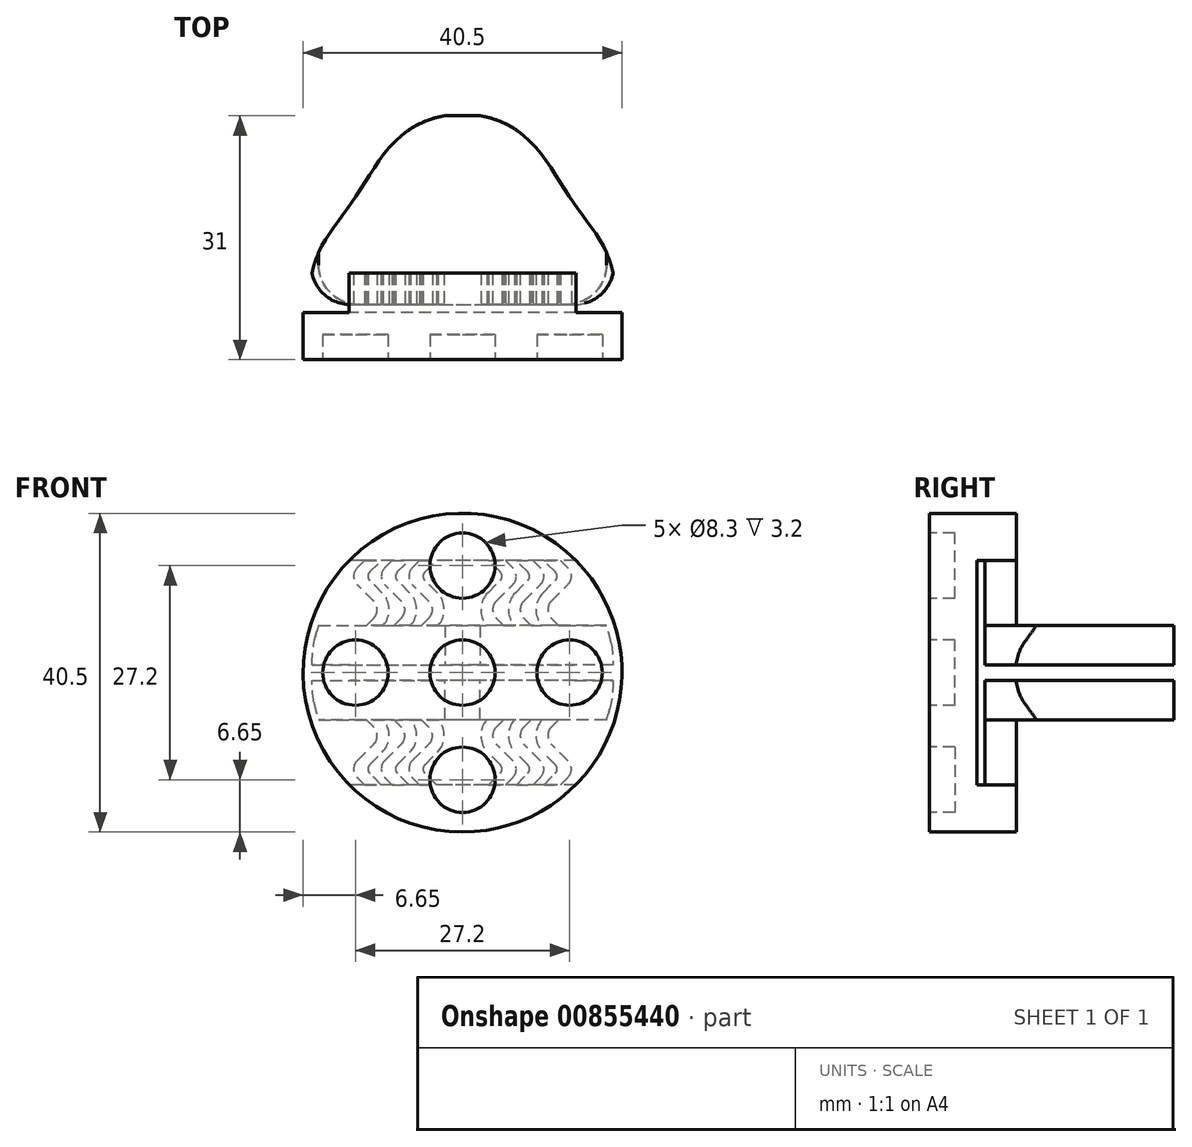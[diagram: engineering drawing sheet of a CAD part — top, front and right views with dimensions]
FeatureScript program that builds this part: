
annotation { "Feature Type Name" : "Feature", "Feature Type Description" : "" }
export const myFeature = defineFeature(function(context is Context, id is Id, definition is map)
    precondition{}
    {
        {
            var Q0;
            Q0=qCreatedBy(makeId("Front.planeOp"),FACE);
            var sketch = newSketch(context, id + "F0", { "sketchPlane" : qUnion([Q0])});
            skCircle(sketch, "E0", {"center": v(0, 0) * mm, "radius": 20.25 * mm});
            skSolve(sketch);
        }
        {
            var Q0;
            Q0 = qSketchRegion(id + "F0", true);
            extrude(context, id + "F1", {"entities" : qUnion([Q0]), "depth" : 6 * mm, "offsetDistance" : 25 * mm});
        }
        {
            var Q0;
            Q0=makeQuery(id+"F1.opExtrude","CAP_FACE",FACE,{"disambiguationData":[OSD([sQuery(id+"F0.wireOp",EDGE,"E0")])],"isStart":false});
            var sketch = newSketch(context, id + "F2", { "sketchPlane" : qUnion([Q0])});
            skCircle(sketch, "E1", {"center": v(0, 0) * mm, "radius": 4.15 * mm});
            skCircle(sketch, "E2", {"center": v(0, 13.6) * mm, "radius": 4.15 * mm});
            skLineSegment(sketch, "E3", {"start": v(-10.79, 17.75) * mm, "end": v(11.03, 17.75) * mm, "construction": true});
            skLineSegment(sketch, "E4", {"start": v(0, 13.6) * mm, "end": v(0, 0) * mm, "construction": true});
            skLineSegment(sketch, "E5", {"start": v(-8.03, 20.25) * mm, "end": v(13.1, 20.25) * mm, "construction": true});
            skCircle(sketch, "E6.1.0", {"center": v(-13.6, 0) * mm, "radius": 4.15 * mm});
            skCircle(sketch, "E6.2.0", {"center": v(0, -13.6) * mm, "radius": 4.15 * mm});
            skCircle(sketch, "E6.3.0", {"center": v(13.6, 0) * mm, "radius": 4.15 * mm});
            skSolve(sketch);
        }
        {
            var Q0;
            Q0 = qSketchRegion(id + "F2", true);
            extrude(context, id + "F3", {"entities" : qUnion([Q0]), "operationType" : NewBodyOperationType.REMOVE, "oppositeDirection" : true, "depth" : 3.2 * mm, "offsetDistance" : 25 * mm});
        }
        {
            var Q0;
            Q0=makeQuery(id+"F1.opExtrude","CAP_FACE",FACE,{"disambiguationData":[OSD([sQuery(id+"F0.wireOp",EDGE,"E0")])],"isStart":true});
            var sketch = newSketch(context, id + "F4", { "sketchPlane" : qUnion([Q0])});
            skArc(sketch, "E7.0", {"start": v(14.39, 14.25) * mm, "mid": v(0, 20.25) * mm, "end": v(-14.39, 14.25) * mm});
            skLineSegment(sketch, "E8", {"start": v(-14.39, 14.25) * mm, "end": v(14.39, 14.25) * mm});
            skLineSegment(sketch, "E9", {"start": v(-14.05, 20.25) * mm, "end": v(12.86, 20.25) * mm, "construction": true});
            skSolve(sketch);
        }
        {
            var Q0;
            Q0 = qSketchRegion(id + "F4", true);
            extrude(context, id + "F5", {"entities" : qUnion([Q0]), "operationType" : NewBodyOperationType.ADD, "depth" : 5 * mm, "offsetDistance" : 25 * mm});
        }
        {
            var Q0;
            Q0=makeQuery(id+"F1.opExtrude","CAP_FACE",FACE,{"disambiguationData":[OSD([sQuery(id+"F0.wireOp",EDGE,"E0")])],"isStart":true});
            var sketch = newSketch(context, id + "F6", { "sketchPlane" : qUnion([Q0])});
            skLineSegment(sketch, "E10", {"start": v(-24.07, 0) * mm, "end": v(27.14, 0) * mm, "construction": true});
            skArc(sketch, "E11.0", {"start": v(18.3, 6) * mm, "mid": v(18.92, 3.53) * mm, "end": v(19.22, 1) * mm});
            skLineSegment(sketch, "E12", {"start": v(-18.3, 6) * mm, "end": v(18.3, 6) * mm});
            skLineSegment(sketch, "E13", {"start": v(-19.22, 1) * mm, "end": v(19.22, 1) * mm});
            skArc(sketch, "E14.trimOffspring", {"start": v(-19.22, 1) * mm, "mid": v(-18.92, 3.53) * mm, "end": v(-18.3, 6) * mm});
            skSolve(sketch);
        }
        {
            var Q0;
            Q0 = qSketchRegion(id + "F6", true);
            extrude(context, id + "F7", {"entities" : qUnion([Q0]), "operationType" : NewBodyOperationType.ADD, "depth" : 25 * mm, "offsetDistance" : 25 * mm});
        }
        {
            var Q0;
            Q0=makeQuery(id+"F1.opExtrude","CAP_FACE",FACE,{"disambiguationData":[OSD([sQuery(id+"F0.wireOp",EDGE,"E0")])],"isStart":true});
            var sketch = newSketch(context, id + "F8", { "sketchPlane" : qUnion([Q0])});
            skArc(sketch, "E15", {"start": v(-13.39, 13.3) * mm, "mid": v(-13.83, 12.25) * mm, "end": v(-13.39, 11.19) * mm});
            skLineSegment(sketch, "E16", {"start": v(-12.44, 14.25) * mm, "end": v(-13.39, 13.3) * mm});
            skLineSegment(sketch, "E17", {"start": v(-13.39, 11.19) * mm, "end": v(-11.27, 9.06) * mm});
            skArc(sketch, "E18", {"start": v(-11.27, 6.94) * mm, "mid": v(-10.83, 8) * mm, "end": v(-11.27, 9.06) * mm});
            skLineSegment(sketch, "E19", {"start": v(-11.27, 6.94) * mm, "end": v(-12.2, 6) * mm});
            skLineSegment(sketch, "E20", {"start": v(-12.33, 12.25) * mm, "end": v(-12.33, 8) * mm, "construction": true});
            skLineSegment(sketch, "E21", {"start": v(-21.46, 14.25) * mm, "end": v(-21.46, 6) * mm, "construction": true});
            skPoint(sketch, "E22", {"position": v(-21.46, 10.12) * mm});
            skPoint(sketch, "E23", {"position": v(-12.33, 10.12) * mm});
            skLineSegment(sketch, "E24", {"start": v(-21.46, 10.12) * mm, "end": v(-12.33, 10.12) * mm, "construction": true});
            skLineSegment(sketch, "E25.0", {"start": v(-10.32, 14.25) * mm, "end": v(-11.8, 12.78) * mm});
            skLineSegment(sketch, "E26.0", {"start": v(-11.8, 11.72) * mm, "end": v(-10.2, 10.12) * mm});
            skArc(sketch, "E27.0", {"start": v(-10.1, 6) * mm, "mid": v(-9.33, 8.08) * mm, "end": v(-10.2, 10.12) * mm});
            skLineSegment(sketch, "E28.trimOffspring", {"start": v(-12.2, 6) * mm, "end": v(-10.1, 6) * mm});
            skPoint(sketch, "E29.0.start.orphan", {"position": v(-18.3, 6) * mm});
            skArc(sketch, "E30", {"start": v(-11.8, 12.78) * mm, "mid": v(-12.02, 12.25) * mm, "end": v(-11.8, 11.72) * mm});
            skLineSegment(sketch, "E31", {"start": v(-12.44, 14.25) * mm, "end": v(-10.32, 14.25) * mm});
            skArc(sketch, "E32.1.0.0", {"start": v(-9.89, 13.3) * mm, "mid": v(-10.33, 12.25) * mm, "end": v(-9.89, 11.19) * mm});
            skPoint(sketch, "E32.1.0.1", {"position": v(-8.83, 10.12) * mm});
            skLineSegment(sketch, "E32.1.0.2", {"start": v(-8.7, 6) * mm, "end": v(-6.6, 6) * mm});
            skArc(sketch, "E32.1.0.3", {"start": v(-6.6, 6) * mm, "mid": v(-5.83, 8.08) * mm, "end": v(-6.7, 10.12) * mm});
            skLineSegment(sketch, "E32.1.0.4", {"start": v(-8.3, 11.72) * mm, "end": v(-6.7, 10.12) * mm});
            skLineSegment(sketch, "E32.1.0.5", {"start": v(-6.82, 14.25) * mm, "end": v(-8.3, 12.78) * mm});
            skArc(sketch, "E32.1.0.6", {"start": v(-7.77, 6.94) * mm, "mid": v(-7.33, 8) * mm, "end": v(-7.77, 9.06) * mm});
            skLineSegment(sketch, "E32.1.0.7", {"start": v(-8.94, 14.25) * mm, "end": v(-6.82, 14.25) * mm});
            skLineSegment(sketch, "E32.1.0.8", {"start": v(-7.77, 6.94) * mm, "end": v(-8.7, 6) * mm});
            skLineSegment(sketch, "E32.1.0.9", {"start": v(-9.89, 11.19) * mm, "end": v(-7.77, 9.06) * mm});
            skLineSegment(sketch, "E32.1.0.10", {"start": v(-8.94, 14.25) * mm, "end": v(-9.89, 13.3) * mm});
            skArc(sketch, "E32.1.0.11", {"start": v(-8.3, 12.78) * mm, "mid": v(-8.52, 12.25) * mm, "end": v(-8.3, 11.72) * mm});
            skArc(sketch, "E32.2.0.0", {"start": v(-6.39, 13.3) * mm, "mid": v(-6.83, 12.25) * mm, "end": v(-6.39, 11.19) * mm});
            skPoint(sketch, "E32.2.0.1", {"position": v(-5.33, 10.12) * mm});
            skLineSegment(sketch, "E32.2.0.2", {"start": v(-5.2, 6) * mm, "end": v(-3.1, 6) * mm});
            skArc(sketch, "E32.2.0.3", {"start": v(-3.1, 6) * mm, "mid": v(-2.33, 8.08) * mm, "end": v(-3.2, 10.12) * mm});
            skLineSegment(sketch, "E32.2.0.4", {"start": v(-4.8, 11.72) * mm, "end": v(-3.2, 10.12) * mm});
            skLineSegment(sketch, "E32.2.0.5", {"start": v(-3.32, 14.25) * mm, "end": v(-4.8, 12.78) * mm});
            skArc(sketch, "E32.2.0.6", {"start": v(-4.27, 6.94) * mm, "mid": v(-3.83, 8) * mm, "end": v(-4.27, 9.06) * mm});
            skLineSegment(sketch, "E32.2.0.7", {"start": v(-5.44, 14.25) * mm, "end": v(-3.32, 14.25) * mm});
            skLineSegment(sketch, "E32.2.0.8", {"start": v(-4.27, 6.94) * mm, "end": v(-5.2, 6) * mm});
            skLineSegment(sketch, "E32.2.0.9", {"start": v(-6.39, 11.19) * mm, "end": v(-4.27, 9.06) * mm});
            skLineSegment(sketch, "E32.2.0.10", {"start": v(-5.44, 14.25) * mm, "end": v(-6.39, 13.3) * mm});
            skArc(sketch, "E32.2.0.11", {"start": v(-4.8, 12.78) * mm, "mid": v(-5.02, 12.25) * mm, "end": v(-4.8, 11.72) * mm});
            skLineSegment(sketch, "E32.direction1", {"start": v(-12.2, 6) * mm, "end": v(-8.7, 6) * mm, "construction": true});
            skLineSegment(sketch, "E33", {"start": v(0, 0) * mm, "end": v(0, 15.57) * mm, "construction": true});
            skLineSegment(sketch, "E34.MirrorCS", {"start": v(7.77, 6.94) * mm, "end": v(8.7, 6) * mm});
            skLineSegment(sketch, "E35.MirrorCS", {"start": v(13.39, 11.19) * mm, "end": v(11.27, 9.06) * mm});
            skLineSegment(sketch, "E36.MirrorCS", {"start": v(4.27, 6.94) * mm, "end": v(5.2, 6) * mm});
            skArc(sketch, "E37.MirrorCS", {"start": v(8.3, 12.78) * mm, "mid": v(8.52, 12.25) * mm, "end": v(8.3, 11.72) * mm});
            skArc(sketch, "E38.MirrorCS", {"start": v(4.8, 12.78) * mm, "mid": v(5.02, 12.25) * mm, "end": v(4.8, 11.72) * mm});
            skArc(sketch, "E39.MirrorCS", {"start": v(11.8, 12.78) * mm, "mid": v(12.02, 12.25) * mm, "end": v(11.8, 11.72) * mm});
            skLineSegment(sketch, "E40.MirrorCS", {"start": v(12.44, 14.25) * mm, "end": v(13.39, 13.3) * mm});
            skLineSegment(sketch, "E41.MirrorCS", {"start": v(11.27, 6.94) * mm, "end": v(12.2, 6) * mm});
            skLineSegment(sketch, "E42.MirrorCS", {"start": v(8.94, 14.25) * mm, "end": v(9.89, 13.3) * mm});
            skLineSegment(sketch, "E43.MirrorCS", {"start": v(5.44, 14.25) * mm, "end": v(6.39, 13.3) * mm});
            skLineSegment(sketch, "E44.MirrorCS", {"start": v(9.89, 11.19) * mm, "end": v(7.77, 9.06) * mm});
            skLineSegment(sketch, "E45.MirrorCS", {"start": v(6.39, 11.19) * mm, "end": v(4.27, 9.06) * mm});
            skLineSegment(sketch, "E46.MirrorCS", {"start": v(12.2, 6) * mm, "end": v(10.1, 6) * mm});
            skArc(sketch, "E47.MirrorCS", {"start": v(3.1, 6) * mm, "mid": v(2.33, 8.08) * mm, "end": v(3.2, 10.12) * mm});
            skLineSegment(sketch, "E48.MirrorCS", {"start": v(8.7, 6) * mm, "end": v(6.6, 6) * mm});
            skLineSegment(sketch, "E49.MirrorCS", {"start": v(11.8, 11.72) * mm, "end": v(10.2, 10.12) * mm});
            skLineSegment(sketch, "E50.MirrorCS", {"start": v(3.32, 14.25) * mm, "end": v(4.8, 12.78) * mm});
            skArc(sketch, "E51.MirrorCS", {"start": v(11.27, 6.94) * mm, "mid": v(10.83, 8) * mm, "end": v(11.27, 9.06) * mm});
            skArc(sketch, "E52.MirrorCS", {"start": v(6.6, 6) * mm, "mid": v(5.83, 8.08) * mm, "end": v(6.7, 10.12) * mm});
            skLineSegment(sketch, "E53.MirrorCS", {"start": v(5.2, 6) * mm, "end": v(3.1, 6) * mm});
            skArc(sketch, "E54.MirrorCS", {"start": v(9.89, 13.3) * mm, "mid": v(10.33, 12.25) * mm, "end": v(9.89, 11.19) * mm});
            skLineSegment(sketch, "E55.MirrorCS", {"start": v(12.2, 6) * mm, "end": v(8.7, 6) * mm, "construction": true});
            skLineSegment(sketch, "E56.MirrorCS", {"start": v(5.44, 14.25) * mm, "end": v(3.32, 14.25) * mm});
            skPoint(sketch, "E57.MirrorP", {"position": v(8.83, 10.12) * mm});
            skPoint(sketch, "E58.MirrorP", {"position": v(5.33, 10.12) * mm});
            skArc(sketch, "E59.MirrorCS", {"start": v(6.39, 13.3) * mm, "mid": v(6.83, 12.25) * mm, "end": v(6.39, 11.19) * mm});
            skLineSegment(sketch, "E60.MirrorCS", {"start": v(8.3, 11.72) * mm, "end": v(6.7, 10.12) * mm});
            skLineSegment(sketch, "E61.MirrorCS", {"start": v(6.82, 14.25) * mm, "end": v(8.3, 12.78) * mm});
            skArc(sketch, "E62.MirrorCS", {"start": v(4.27, 6.94) * mm, "mid": v(3.83, 8) * mm, "end": v(4.27, 9.06) * mm});
            skLineSegment(sketch, "E63.MirrorCS", {"start": v(10.32, 14.25) * mm, "end": v(11.8, 12.78) * mm});
            skLineSegment(sketch, "E64.MirrorCS", {"start": v(4.8, 11.72) * mm, "end": v(3.2, 10.12) * mm});
            skLineSegment(sketch, "E65.MirrorCS", {"start": v(12.33, 12.25) * mm, "end": v(12.33, 8) * mm, "construction": true});
            skLineSegment(sketch, "E66.MirrorCS", {"start": v(8.94, 14.25) * mm, "end": v(6.82, 14.25) * mm});
            skArc(sketch, "E67.MirrorCS", {"start": v(7.77, 6.94) * mm, "mid": v(7.33, 8) * mm, "end": v(7.77, 9.06) * mm});
            skArc(sketch, "E68.MirrorCS", {"start": v(10.1, 6) * mm, "mid": v(9.33, 8.08) * mm, "end": v(10.2, 10.12) * mm});
            skArc(sketch, "E69.MirrorCS", {"start": v(13.39, 13.3) * mm, "mid": v(13.83, 12.25) * mm, "end": v(13.39, 11.19) * mm});
            skLineSegment(sketch, "E70.MirrorCS", {"start": v(12.44, 14.25) * mm, "end": v(10.32, 14.25) * mm});
            skPoint(sketch, "E71.MirrorP", {"position": v(12.33, 10.12) * mm});
            skSolve(sketch);
        }
        {
            var Q0;
            Q0 = qSketchRegion(id + "F8", true);
            var Q1;
            Q1=makeQuery(id+"F5.opExtrude","CAP_FACE",FACE,{"disambiguationData":[OSD([sQuery(id+"F4.wireOp",EDGE,"E7.0"),sQuery(id+"F4.wireOp",EDGE,"E8")])],"isStart":false});
            extrude(context, id + "F9", {"entities" : qUnion([Q0]), "operationType" : NewBodyOperationType.ADD, "endBound" : BoundingType.UP_TO_SURFACE, "depth" : 25 * mm, "endBoundEntityFace" : qUnion([Q1]), "offsetDistance" : 25 * mm});
        }
        {
            var Q0;
            Q0=makeQuery(id+"F7.opExtrude","SWEPT_FACE",FACE,{"disambiguationData":[OSD([sQuery(id+"F6.wireOp",EDGE,"E13")])]});
            var sketch = newSketch(context, id + "F10", { "sketchPlane" : qUnion([Q0])});
            skFitSpline(sketch, "E72", {"points": [v(19.22, -4.34) * mm, v(13.54, -14.74) * mm, v(2.23, -25) * mm], "startDerivative": vector(-3.66, -27.38) * mm, "endDerivative": vector(-36.07, -5.9) * mm});
            skLineSegment(sketch, "E73", {"start": v(0, 0) * mm, "end": v(0, -11.1) * mm, "construction": true});
            skFitSpline(sketch, "E74.MirrorCS", {"points": [v(-19.22, -4.34) * mm, v(-13.54, -14.74) * mm, v(-2.23, -25) * mm], "startDerivative": vector(3.66, -27.38) * mm, "endDerivative": vector(36.07, -5.9) * mm});
            skSolve(sketch);
        }
        {
            var Q0;
            Q0 = qSketchRegion(id + "F10", true);
            var Q1;
            {var subQ0=sQuery(id+"F10.wireOp",EDGE,"E72");Q1=makeQuery(id+"F10.imprint","IMPRINT",FACE,{"disambiguationData":[TD([[makeQuery(id+"F10.imprint","IMPRINT",EDGE,{"derivedFrom":subQ0}),1.0]])]});}
            var Q2;
            {var subQ0=sQuery(id+"F10.wireOp",EDGE,"E74.MirrorCS");Q2=makeQuery(id+"F10.imprint","IMPRINT",FACE,{"disambiguationData":[TD([[makeQuery(id+"F10.imprint","IMPRINT",EDGE,{"derivedFrom":subQ0}),-1.0]])]});}
            extrude(context, id + "F11", {"entities" : qUnion([Q0, Q1, Q2]), "operationType" : NewBodyOperationType.REMOVE, "oppositeDirection" : true, "depth" : 25 * mm, "offsetDistance" : 25 * mm});
        }
        {
            var Q0;
            {var subQ0=sQuery(id+"F0.wireOp",EDGE,"E0");Q0=makeQuery(id+"F9.boolean.opBoolean","SPLIT",FACE,{"disambiguationData":[TD([makeQuery(id+"F1.opExtrude","SWEPT_FACE",FACE,{"disambiguationData":[OSD([subQ0])]})])],"derivedFrom":makeQuery(id+"F1.opExtrude","CAP_FACE",FACE,{"disambiguationData":[OSD([subQ0])],"isStart":true})});}
            var sketch = newSketch(context, id + "F12", { "sketchPlane" : qUnion([Q0])});
            skLineSegment(sketch, "E75", {"start": v(-28.59, 0) * mm, "end": v(23.3, 0) * mm});
            skSolve(sketch);
        }
        {
            var Q0;
            Q0 = qSketchRegion(id + "F12", true);
            var Q1;
            {var subQ0=sQuery(id+"F12.wireOp",EDGE,"E75");var subQ1=makeQuery(id+"F1.opExtrude","CAP_EDGE",EDGE,{"disambiguationData":[OSD([sQuery(id+"F0.wireOp",EDGE,"E0")])],"isStart":true});var subQ2=makeQuery(id+"F12.imprint","INTERSECT",VERTEX,{"disambiguationData":[OD(0.0)],"derivedFrom":[subQ1,subQ0]});Q1=makeQuery(id+"F12.imprint","IMPRINT",FACE,{"disambiguationData":[TD([[makeQuery(id+"F12.imprint","IMPRINT",EDGE,{"disambiguationData":[TD([[subQ2,-1.0]])],"derivedFrom":subQ0}),-1.0]])]});}
            extrude(context, id + "F13", {"entities" : qUnion([Q0, Q1]), "operationType" : NewBodyOperationType.REMOVE, "oppositeDirection" : true, "depth" : 25 * mm, "offsetDistance" : 25 * mm});
        }
        {
            var Q0;
            Q0=makeQuery(id+"F1.opExtrude","SWEPT_BODY",BODY,{"disambiguationData":[OSD([sQuery(id+"F0.wireOp",EDGE,"E0")])]});
            var Q1;
            Q1=makeQuery(id+"F13.boolean.opBoolean","COPY",FACE,{"derivedFrom":makeQuery(id+"F13.opExtrude","SWEPT_FACE",FACE,{"disambiguationData":[OSD([sQuery(id+"F12.wireOp",EDGE,"E75")])]})});
            mirror(context, id + "F14", {"operationType" : NewBodyOperationType.ADD, "entities" : qUnion([Q0]), "mirrorPlane" : qUnion([Q1])});
        }
        {
            var Q0;
            Q0=qCreatedBy(makeId("Right.planeOp"),FACE);
            var sketch = newSketch(context, id + "F15", { "sketchPlane" : qUnion([Q0])});
            skLineSegment(sketch, "E76.bottom", {"start": v(1, 14.25) * mm, "end": v(0, 14.25) * mm});
            skLineSegment(sketch, "E76.top", {"start": v(1, -14.25) * mm, "end": v(0, -14.25) * mm});
            skLineSegment(sketch, "E76.left", {"start": v(1, 14.25) * mm, "end": v(1, -14.25) * mm});
            skLineSegment(sketch, "E76.right", {"start": v(0, 14.25) * mm, "end": v(0, -14.25) * mm});
            skSolve(sketch);
        }
        {
            var Q0;
            Q0 = qSketchRegion(id + "F15", true);
            extrude(context, id + "F16", {"entities" : qUnion([Q0]), "operationType" : NewBodyOperationType.REMOVE, "endBound" : BoundingType.THROUGH_ALL, "oppositeDirection" : true, "depth" : 25 * mm, "offsetDistance" : 25 * mm, "hasSecondDirection" : true, "secondDirectionBound" : SecondDirectionBoundingType.THROUGH_ALL, "secondDirectionOppositeDirection" : false, "secondDirectionDepth" : 25 * mm});
        }
        {
            var Q0;
            Q0=makeQuery(id+"F16.boolean.opBoolean","INTERSECT",EDGE,{"derivedFrom":[makeQuery(id+"F7.opExtrude","SWEPT_FACE",FACE,{"disambiguationData":[OSD([sQuery(id+"F6.wireOp",EDGE,"E14.trimOffspring")])]}),makeQuery(id+"F16.opExtrude","SWEPT_FACE",FACE,{"disambiguationData":[OSD([sQuery(id+"F15.wireOp",EDGE,"E76.left")])]})]});
            var Q1;
            Q1=makeQuery(id+"F16.boolean.opBoolean","INTERSECT",EDGE,{"derivedFrom":[makeQuery(id+"F14.opPattern","COPY",FACE,{"derivedFrom":makeQuery(id+"F7.opExtrude","SWEPT_FACE",FACE,{"disambiguationData":[OSD([sQuery(id+"F6.wireOp",EDGE,"E14.trimOffspring")])]}),"instanceName":"1"}),makeQuery(id+"F16.opExtrude","SWEPT_FACE",FACE,{"disambiguationData":[OSD([sQuery(id+"F15.wireOp",EDGE,"E76.left")])]})]});
            var Q2;
            Q2=makeQuery(id+"F16.boolean.opBoolean","INTERSECT",EDGE,{"derivedFrom":[makeQuery(id+"F14.opPattern","COPY",FACE,{"derivedFrom":makeQuery(id+"F7.opExtrude","SWEPT_FACE",FACE,{"disambiguationData":[OSD([sQuery(id+"F6.wireOp",EDGE,"E11.0")])]}),"instanceName":"1"}),makeQuery(id+"F16.opExtrude","SWEPT_FACE",FACE,{"disambiguationData":[OSD([sQuery(id+"F15.wireOp",EDGE,"E76.left")])]})]});
            var Q3;
            Q3=makeQuery(id+"F16.boolean.opBoolean","INTERSECT",EDGE,{"derivedFrom":[makeQuery(id+"F7.opExtrude","SWEPT_FACE",FACE,{"disambiguationData":[OSD([sQuery(id+"F6.wireOp",EDGE,"E11.0")])]}),makeQuery(id+"F16.opExtrude","SWEPT_FACE",FACE,{"disambiguationData":[OSD([sQuery(id+"F15.wireOp",EDGE,"E76.left")])]})]});
            fillet(context, id + "F17", {"entities" : qUnion([Q0, Q1, Q2, Q3]), "radius" : 5 * mm, "tangentPropagation" : true, "allowEdgeOverflow" : false});
        }
    });
